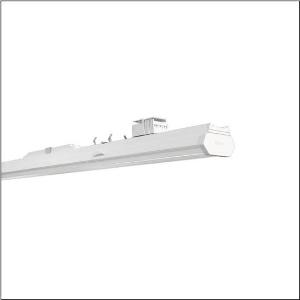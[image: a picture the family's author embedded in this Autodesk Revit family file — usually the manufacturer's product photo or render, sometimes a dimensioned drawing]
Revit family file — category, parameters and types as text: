
# Revit family: licross_r__21_protected_mo_52tp12dn4a5gd_0331
name_source: partatom
category: Lighting Fixtures
units: mm (PartAtom-declared; Revit-internal decimal feet)

## family parameters
Cut with Voids When Loaded = No
Host = Face
Light Source = No
Part Type = Normal
Room Calculation Point = No
Round Connector Dimension = Use Diameter
Shared = No

## types (1)
- --- (1 x LED, 1610 lm, 10.2 W, 4000K)
    Apparent Load = 10 VA
    CIE Flux Codes = 73 92 98 99 100
    Color Rendering = 80
    Color Temperature = 4000K
    Default Elevation = 1800 mm
    Description = Licross® 21 Protected MO, luminaire insert, of sheet steel, galvanised, coil coated, white, length: 1.500mm, width: 90mm, height: 103mm, LED rated luminous flux: 10.700lm, light colour: 840, control gear: DALI 2 (for two DALI lines), with plug, 6-pole, with phase selection, mains connection: 220..240V, AC/DC, 0/50..60Hz, rated input power: 62W, without changeover relay, for emergency light function, for central battery installations according to DIN EN 60598-2-22, halogen-free wiring, primary light control with lens, of plastic, primary optical cover: cover, of PMMA, light emission: direct distribution, primary light characteristic: symmetric, protection rating (complete): IP64, insulation class (complete): insulation class I (protective earthing), certification: CE, ENEC, VDE, UKCA, protection symbol: D if used in an environment with conductive dust loads with corresponding accessories, impact resistance: IK06, permissible ambient temperature for indoor applications: -25..+35°C, standard: EN 60598-2-22, corresponds to IFS (International Featured Standards) requirements for safety and quality in the food industry, reducing of maximum allowable ambient temperature of 5°C with ceiling mounting, LABS conformity tested according to VDMA 24364:2018-05, packaging unit: 1 piece
    Height = 92 mm
    Lamp = 1 x LED
    Lamp Light Flux = 1610 lm
    Lamp Power = 10.2 W
    Lamp count = 1
    Length = 1500 mm
    Luminous efficacy = 158 lm/W
    Manufacturer = Siteco
    ModVariant = No
    Model = 52TP12DN4A5GD
    Mounting Place = Ceiling
    Mounting Type = Pendant
    Number of Poles = 1
    OnlyDefault = Yes
    Power Factor = 1
    Product Name = Licross® 21 Protected MO
    Product group = luminaire insert
    ProductGroupID = 901
    Protection Class = Protection class I
    Protection Degree = IP 64
    RLX_Detail_Level = 1
    RLX_Emergency_Light_Flux = 0 lm
    RLX_Emergency_Type = 0
    RLX_Emergency_Type_DB = No
    RlxData = <blob elided: 24941 chars, md5=96b2aec9>
    Socket = socket
    Standby Power = 0 W
    System Light Flux = 1610 lm
    System Power = 10 W
    Type Comments = : DC mode (central or group accumulator) initial emergency light level
    Type Image = l_1256148.jpg
    URL = http://relux.com
    VarID = @adj_085105
    Voltage = 0 V
    Weight = 0.00 kg
    Width = 88 mm

## geometry (parser evidence)
native form markers: Blend x4, Sweep x9
no freeform markers — native parametric forms only
